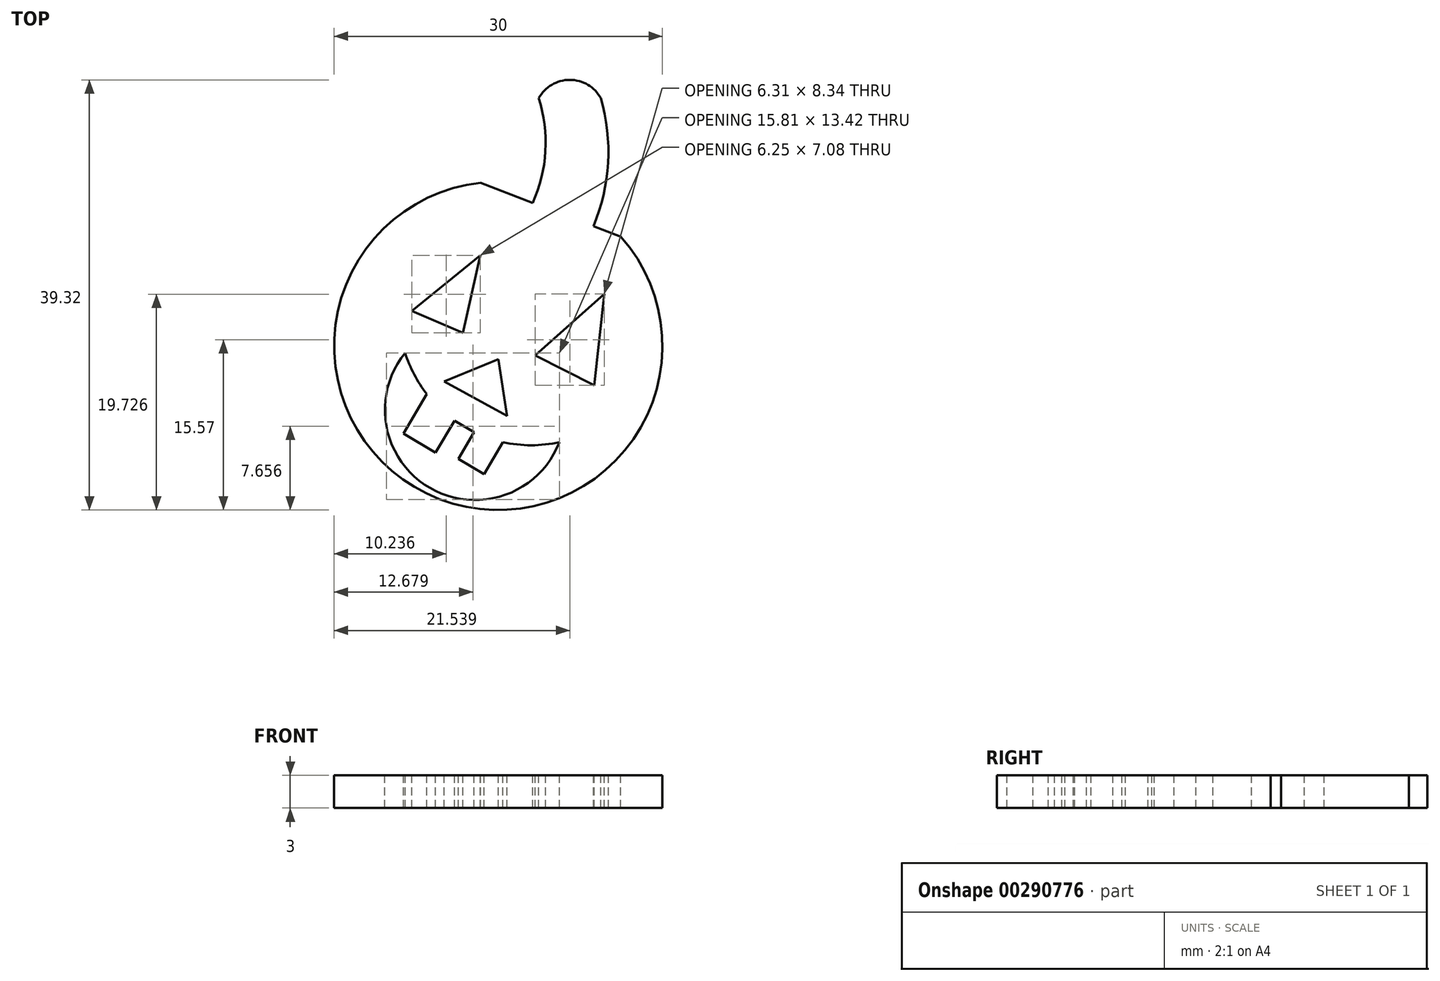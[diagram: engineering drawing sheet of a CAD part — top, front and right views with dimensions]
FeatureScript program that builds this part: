
annotation { "Feature Type Name" : "Feature", "Feature Type Description" : "" }
export const myFeature = defineFeature(function(context is Context, id is Id, definition is map)
    precondition{}
    {
        {
            var Q0;
            Q0=qCreatedBy(makeId("Top.planeOp"),FACE);
            var sketch = newSketch(context, id + "F0", { "sketchPlane" : qUnion([Q0])});
            skArc(sketch, "E0", {"start": v(-1.62, 14.91) * mm, "mid": v(-5.38, -14) * mm, "end": v(11.19, 10) * mm});
            skLineSegment(sketch, "E1", {"start": v(-1.62, 14.91) * mm, "end": v(3.15, 13.08) * mm});
            skArc(sketch, "E2", {"start": v(3.15, 13.08) * mm, "mid": v(4.3, 17.81) * mm, "end": v(3.7, 22.64) * mm});
            skArc(sketch, "E3", {"start": v(8.7, 10.95) * mm, "mid": v(10.04, 16.74) * mm, "end": v(9.37, 22.64) * mm});
            skArc(sketch, "E4", {"start": v(9.37, 22.64) * mm, "mid": v(6.53, 24.32) * mm, "end": v(3.7, 22.64) * mm});
            skLineSegment(sketch, "E5.trimOffspring", {"start": v(8.7, 10.95) * mm, "end": v(11.19, 10) * mm});
            skLineSegment(sketch, "E6", {"start": v(-7.89, 3.18) * mm, "end": v(-1.64, 8.27) * mm});
            skLineSegment(sketch, "E7", {"start": v(-1.64, 8.27) * mm, "end": v(-3.22, 1.19) * mm});
            skLineSegment(sketch, "E8", {"start": v(-3.22, 1.19) * mm, "end": v(-7.89, 3.18) * mm});
            skArc(sketch, "E9", {"start": v(-8.51, -0.63) * mm, "mid": v(-6.25, -12.98) * mm, "end": v(5.58, -8.8) * mm});
            skArc(sketch, "E10", {"start": v(-8.51, -0.63) * mm, "mid": v(-7.69, -2.6) * mm, "end": v(-6.53, -4.4) * mm});
            skLineSegment(sketch, "E11", {"start": v(3.39, -0.87) * mm, "end": v(8.78, -3.6) * mm});
            skLineSegment(sketch, "E12", {"start": v(8.78, -3.6) * mm, "end": v(9.7, 4.74) * mm});
            skLineSegment(sketch, "E13", {"start": v(9.7, 4.74) * mm, "end": v(3.39, -0.87) * mm});
            skLineSegment(sketch, "E14", {"start": v(-4.95, -3.25) * mm, "end": v(0.8, -6.4) * mm});
            skLineSegment(sketch, "E15", {"start": v(0.8, -6.4) * mm, "end": v(0, -1.22) * mm});
            skLineSegment(sketch, "E16", {"start": v(0, -1.22) * mm, "end": v(-4.95, -3.25) * mm});
            skLineSegment(sketch, "E17", {"start": v(-6.53, -4.4) * mm, "end": v(-8.66, -8.01) * mm});
            skLineSegment(sketch, "E18", {"start": v(-8.66, -8.01) * mm, "end": v(-5.73, -9.75) * mm});
            skLineSegment(sketch, "E19", {"start": v(-5.73, -9.75) * mm, "end": v(-4, -6.83) * mm});
            skLineSegment(sketch, "E20", {"start": v(-4, -6.83) * mm, "end": v(-2.22, -7.9) * mm});
            skLineSegment(sketch, "E21", {"start": v(-2.22, -7.9) * mm, "end": v(-3.65, -10.32) * mm});
            skLineSegment(sketch, "E22", {"start": v(-3.65, -10.32) * mm, "end": v(-1.3, -11.71) * mm});
            skLineSegment(sketch, "E23", {"start": v(-1.3, -11.71) * mm, "end": v(0.42, -8.8) * mm});
            skArc(sketch, "E24.trimOffspring", {"start": v(-4, -6.83) * mm, "mid": v(-3.14, -7.4) * mm, "end": v(-2.22, -7.9) * mm});
            skArc(sketch, "E25.trimOffspring", {"start": v(0.42, -8.8) * mm, "mid": v(3, -9.08) * mm, "end": v(5.58, -8.8) * mm});
            skSolve(sketch);
        }
        {
            var Q0;
            Q0 = qSketchRegion(id + "F0", true);
            extrude(context, id + "F1", {"entities" : qUnion([Q0]), "oppositeDirection" : true, "depth" : 3 * mm});
        }
    });
